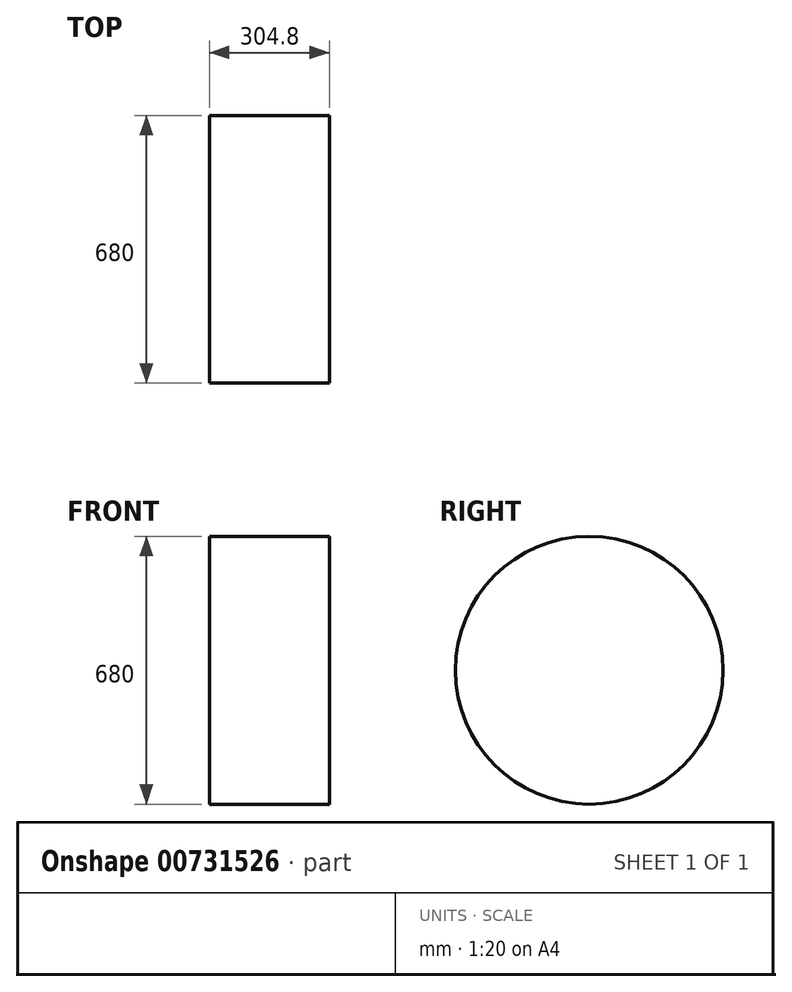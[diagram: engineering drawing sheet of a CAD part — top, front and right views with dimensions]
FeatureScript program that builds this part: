
annotation { "Feature Type Name" : "Feature", "Feature Type Description" : "" }
export const myFeature = defineFeature(function(context is Context, id is Id, definition is map)
    precondition{}
    {
        {
            var Q0;
            Q0=qCreatedBy(makeId("Right.planeOp"), FACE);
            var sketch = newSketch(context, id + "F0", { "sketchPlane" : qUnion([Q0])});
            skCircle(sketch, "E0", {"center": v(0, 0) * mm, "radius": 340 * mm});
            skSolve(sketch);
        }
        {
            var Q0;
            Q0 = qSketchRegion(id + "F0", true);
            extrude(context, id + "F1", {"entities" : qUnion([Q0]), "depth" : 304.8 * mm, "offsetDistance" : 25 * mm});
        }
    });
